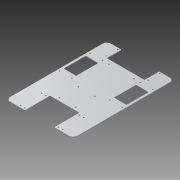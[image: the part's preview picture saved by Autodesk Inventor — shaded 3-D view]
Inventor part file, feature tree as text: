
AUTODESK INVENTOR PART (.ipt)
format: ipt  version: 2015 (Build 190159000, 159)  size: 265,216 bytes
history: native  units: mm
features: sketch x9, extrude x5, hole x5, fillet x3, other x1
ambient origin geometry x8: Origin, YZ Plane, XZ Plane, XY Plane, X Axis, Y Axis, Z Axis, Center Point
bodies: Body1 (feature_tree)
feature tree (23):
  other  "ソリッド1"
  extrude  "押し出し1"  Depth=160.0mm
  hole  "穴1"  [1 undecoded]
  extrude  "押し出し2"  Depth=1.5mm TaperAngle=0.0deg
  fillet  "フィレット1"  Radius=5.0mm
  extrude  "押し出し3"  Depth=5.0mm
  hole  "穴3"  [1 undecoded]
  hole  "穴4"  [1 undecoded]
  extrude  "押し出し4"  Depth=5.0mm
  extrude  "押し出し5"  Depth=73.0mm
  hole  "穴6"  [1 undecoded]
  fillet  "フィレット4"  Radius=30.0mm
  fillet  "フィレット5"  Radius=5.0mm
  hole  "穴7"  [1 undecoded]
  sketch  "スケッチ1"
  sketch  "スケッチ2"
  sketch  "スケッチ4"
  sketch  "スケッチ5"
  sketch  "スケッチ7"
  sketch  "スケッチ10"
  sketch  "スケッチ11"
  sketch  "スケッチ12"
  sketch  "スケッチ13"
note: 5 required parameter values undecoded (feature->parameter linkage not recoverable at this tier; creation-order binding heuristic only, values carry confidence <= 0.55)
